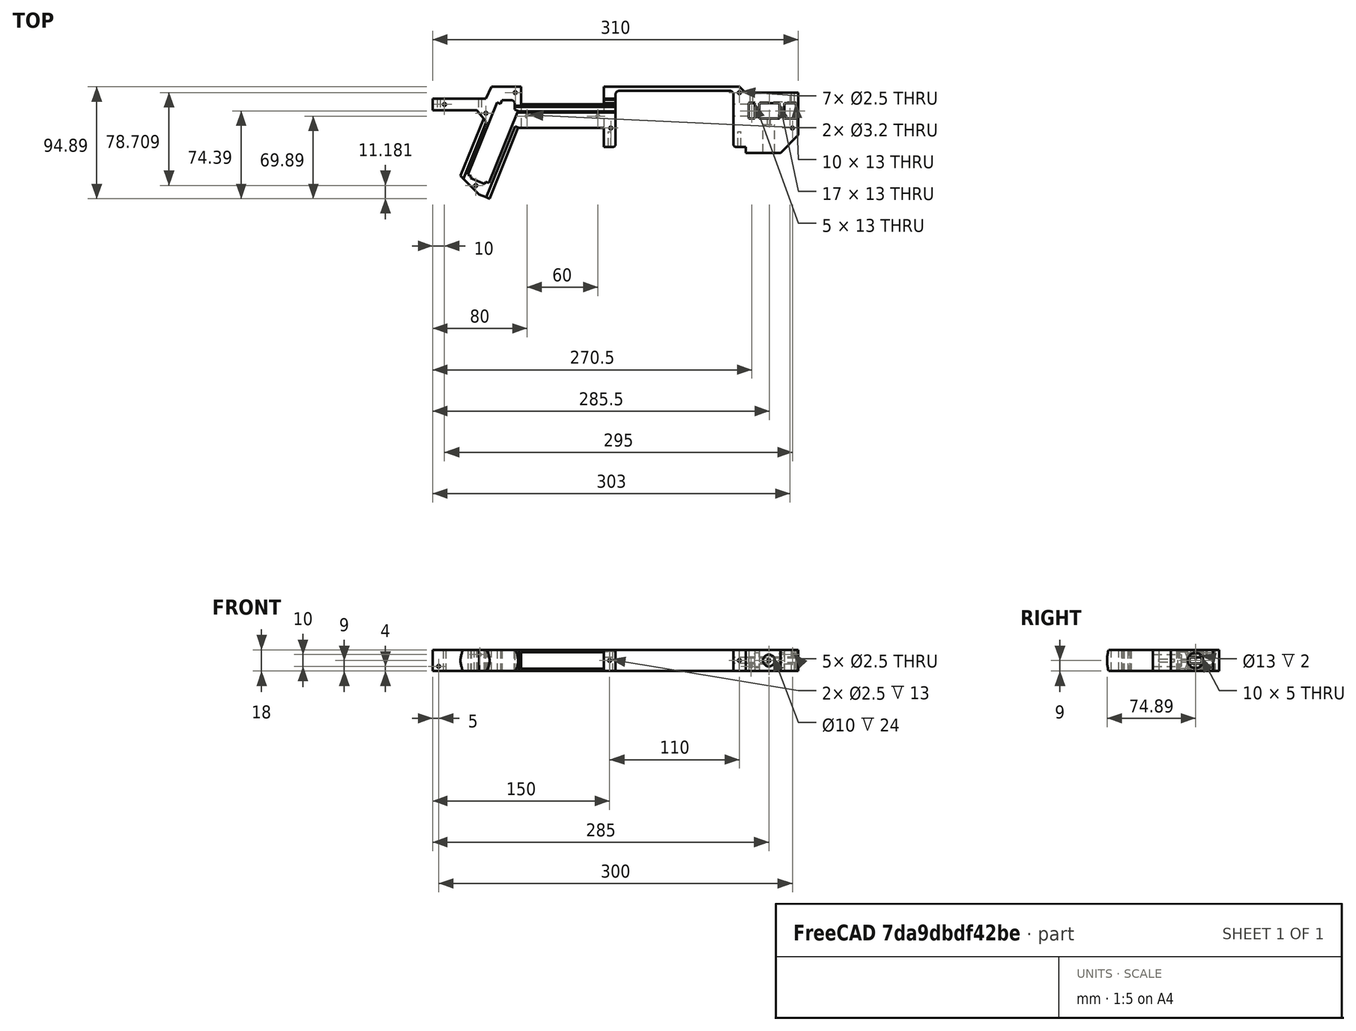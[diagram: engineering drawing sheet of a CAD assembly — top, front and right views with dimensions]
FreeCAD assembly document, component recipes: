
FREECAD ASSEMBLY — COMPONENT RECIPES ("FrameUpper.stl")

This assembly document has 2 components, labeled P0..P1 below (a component is one placed body or linked part). 1 of them carries a construction recipe — the FreeCAD feature program that regenerates the part from scratch, quoted from this document or its linked companion documents; the rest are supplied as boundary geometry only. No exploded tour is included for this assembly.
COMPONENT P0 — recipe-attached ("SizeRequirements", modeled in this document).
Construction recipe (the document's own serialized feature program — sketch geometry with constraints, then the solid features built on it; lengths are millimeters unless a unit is written):

FEATURE [Sketcher::SketchObject] Sketch
  ArcFitTolerance = 1e-06
  AttachmentSupport = -> [XY_Plane001]
  FullyConstrained = true
  MakeInternals = false
  MapMode = 5
  sketch-geometry (17):
    g0: LineSegment StartX=10 StartY=30 StartZ=0 EndX=10 EndY=15 EndZ=0
    g1: LineSegment StartX=10 StartY=15 StartZ=0 EndX=-60 EndY=15 EndZ=0
    g2: LineSegment StartX=-60 StartY=15 StartZ=0 EndX=-60 EndY=30 EndZ=0
    g3: LineSegment StartX=-60 StartY=30 StartZ=0 EndX=-85 EndY=30 EndZ=0
    g4: LineSegment StartX=-85 StartY=30 StartZ=0 EndX=-90 EndY=20 EndZ=0
    g5: LineSegment StartX=-90 StartY=20 StartZ=0 EndX=-135 EndY=20 EndZ=0
    g6: LineSegment StartX=-135 StartY=20 StartZ=0 EndX=-135 EndY=10 EndZ=0
    g7: LineSegment StartX=-135 StartY=10 StartZ=0 EndX=-60 EndY=10 EndZ=0
    g8: LineSegment StartX=-60 StartY=-5 StartZ=0 EndX=10 EndY=-5 EndZ=0
    g9: LineSegment StartX=125 StartY=30 StartZ=0 EndX=10 EndY=30 EndZ=0
    g10: LineSegment StartX=175 StartY=25 StartZ=0 EndX=130 EndY=25 EndZ=0
    g11: LineSegment StartX=130 StartY=25 StartZ=0 EndX=125 EndY=30 EndZ=0
    g12: LineSegment StartX=160 StartY=-26 StartZ=0 EndX=10 EndY=-26 EndZ=0
    g13: LineSegment StartX=10 StartY=-5 StartZ=0 EndX=10 EndY=-26 EndZ=0
    g14: LineSegment StartX=-60 StartY=-5 StartZ=0 EndX=-60 EndY=10 EndZ=0
    g15: LineSegment StartX=160 StartY=-26 StartZ=0 EndX=175 EndY=-11 EndZ=0
    g16: LineSegment StartX=175 StartY=-11 StartZ=0 EndX=175 EndY=25 EndZ=0
  constraints (51):
    c: Coincident(g0,g1)
    c: Horizontal(g1)
    c: Coincident(g1,g2)
    c: Coincident(g2,g3)
    c: Horizontal(g3)
    c: Coincident(g3,g4)
    c: Coincident(g4,g5)
    c: Horizontal(g5)
    c: Coincident(g5,g6)
    c: Coincident(g6,g7)
    c: Coincident(g9,g0)
    c: Horizontal(g9)
    c: Horizontal(g2,g0)
    c: DistanceX(g4,g3) = 5
    c: DistanceX(g3,g3) = 25
    c: DistanceY(g-1,g1) = 15
    c: DistanceY(g-1,g3) = 30
    c: Coincident(g10,g11)
    c: Coincident(g11,g9)
    c: DistanceY(g11,g11) = 5
    c: DistanceX(g11,g11) = 5
    c: DistanceX(g10,g10) = 45
    c: Horizontal(g10)
    c: DistanceX(g5,g5) = 45
    c: Vertical(g6)
    c: DistanceX(g-1,g10) = 175
    c: Horizontal(g7)
    c: Horizontal(g8)
    c: DistanceY(g8,g-1) = 5
    c: Horizontal(g12)
    c: DistanceY(g12,g-1) = 26
    c: Coincident(g13,g8)
    c: Coincident(g13,g12)
    c: Vertical(g2)
    c: Coincident(g14,g8)
    c: Vertical(g14)
    c: Coincident(g14,g7)
    c: DistanceY(g-1,g6) = 10
    c: DistanceY(g4,g4) = 10
    c: DistanceX(g1,g8) = 70
    c: DistanceX(g1,g-1) = 60
    c: DistanceX(g8,g1) = 0
    c: DistanceX(g1,g1) = 70
    c: Vertical(g0)
    c: Vertical(g13)
    c: Coincident(g15,g12)
    c: Coincident(g16,g15)
    c: Coincident(g16,g10)
    c: Vertical(g16)
    c: Angle(g15,g16) = 0.785398
    c: DistanceX(g12,g15) = 15
FEATURE [PartDesign::Pad] Pad
  Direction = (0,0,1)
  Length = 18
  Length2 = 10
  Midplane = true
  Profile = -> Sketch
  ReferenceAxis = -> Sketch [N_Axis]
  Refine = true
  Suppressed = false
  Type = 0
FEATURE [PartDesign::Plane] DatumPlane  label="HandgripRefBase"
  AttachmentOffset = pos=(0,97,50) rot=(-1,0,0;0.383972rad)
  AttachmentSupport = -> [Z_Axis001]
  Length = 75.4155
  MapMode = 2
  Placement = pos=(-97,-50,0) rot=(0.488067,-0.723589,0.488067;1.88883rad)
  ResizeMode = 0
  Width = 348.389
FEATURE [Sketcher::SketchObject] Sketch001
  ArcFitTolerance = 1e-06
  AttachmentSupport = -> [DatumPlane]
  FullyConstrained = true
  MakeInternals = false
  MapMode = 5
  Placement = pos=(-97,-50,0) rot=(0.488067,-0.723589,0.488067;1.88883rad)
  sketch-geometry (7):
    g0: LineSegment StartX=-9 StartY=12 StartZ=0 EndX=-9 EndY=-12 EndZ=0
    g1: LineSegment StartX=9 StartY=12 StartZ=0 EndX=9 EndY=-12 EndZ=0
    g2: ArcOfCircle CenterX=0 CenterY=4e-16 CenterZ=0 NormalX=0 NormalY=0 NormalZ=1 AngleXU=0 Radius=15 StartAngle=0.927295 EndAngle=2.2143
    g3: ArcOfCircle CenterX=0 CenterY=0 CenterZ=0 NormalX=0 NormalY=0 NormalZ=1 AngleXU=0 Radius=15 StartAngle=4.06889 EndAngle=5.35589
    g4: GeomPoint X=0 Y=15 Z=0
    g5: GeomPoint X=0 Y=-15 Z=0
    g6: Circle [constr] CenterX=0 CenterY=4e-16 CenterZ=0 NormalX=0 NormalY=0 NormalZ=1 AngleXU=0 Radius=15
  constraints (20):
    c: Vertical(g0)
    c: Vertical(g1)
    c: PointOnObject(g2,g-2)
    c: Coincident(g2,g0)
    c: Coincident(g2,g1)
    c: Coincident(g3,g1)
    c: Coincident(g3,g0)
    c: Equal(g3,g2)
    c: Distance(g0,g1) = 18
    c: Horizontal(g0,g1)
    c: PointOnObject(g4,g2)
    c: PointOnObject(g5,g3)
    c: Vertical(g5,g-1)
    c: Vertical(g-1,g4)
    c: DistanceY(g5,g4) = 30
    c: DistanceY(g1,g1) = 24
    c: Coincident(g6,g2)
    c: PointOnObject(g1,g6)
    c: PointOnObject(g0,g6)
    c: Coincident(g3,g-1)
FEATURE [PartDesign::Pad] Pad001  label="HadngripTube"
  BaseFeature = -> Pad
  Direction = (-0.374607,-0.927184,0)
  Length = 70
  Length2 = 10
  Profile = -> Sketch001
  ReferenceAxis = -> Sketch001 [N_Axis]
  Refine = true
  Reversed = true
  Suppressed = false
  Type = 4
FEATURE [PartDesign::Plane] DatumPlane001  label="HandgripRefFlat"
  AttachmentOffset = pos=(0,0,0) rot=(0,1,0;1.5708rad)
  AttachmentSupport = -> [DatumPlane]
  Length = 255.46
  MapMode = 5
  Placement = pos=(-97,-50,0) rot=(0,0,1;1.18682rad)
  ResizeMode = 0
  Width = 374.324
FEATURE [Sketcher::SketchObject] Sketch002
  ArcFitTolerance = 1e-06
  AttachmentSupport = -> [DatumPlane001]
  FullyConstrained = true
  MakeInternals = false
  MapMode = 5
  Placement = pos=(-97,-50,0) rot=(0,0,1;1.18682rad)
  sketch-geometry (14):
    g0: LineSegment StartX=2 StartY=-9.5 StartZ=0 EndX=68 EndY=-9.5 EndZ=0
    g1: LineSegment StartX=68 StartY=9.5 StartZ=0 EndX=2 EndY=9.5 EndZ=0
    g2: LineSegment StartX=2 StartY=9.5 StartZ=0 EndX=2 EndY=6.5 EndZ=0
    g3: LineSegment StartX=2 StartY=6.5 StartZ=0 EndX=0 EndY=6.5 EndZ=0
    g4: LineSegment StartX=0 StartY=6.5 StartZ=0 EndX=0 EndY=-6.5 EndZ=0
    g5: LineSegment StartX=0 StartY=-6.5 StartZ=0 EndX=2 EndY=-6.5 EndZ=0
    g6: LineSegment StartX=2 StartY=-6.5 StartZ=0 EndX=2 EndY=-9.5 EndZ=0
    g7: LineSegment StartX=68 StartY=-9.5 StartZ=0 EndX=68 EndY=-6.5 EndZ=0
    g8: LineSegment StartX=68 StartY=9.5 StartZ=0 EndX=68 EndY=6.5 EndZ=0
    g9: LineSegment StartX=68 StartY=6.5 StartZ=0 EndX=71.3759 EndY=6.5 EndZ=0
    g10: LineSegment StartX=71.3759 StartY=6.5 StartZ=0 EndX=74.2937 EndY=-0.721596 EndZ=0
    g11: LineSegment StartX=72.6359 StartY=-4.62697 StartZ=0 EndX=68 EndY=-6.5 EndZ=0
    g12: ArcOfCircle CenterX=71.5121 CenterY=-1.84542 CenterZ=0 NormalX=0 NormalY=0 NormalZ=1 AngleXU=0 Radius=3 StartAngle=5.09636 EndAngle=6.66716
    g13: GeomPoint [constr] X=75.4175 Y=-3.50315 Z=0
  constraints (39):
    c: Horizontal(g0)
    c: Horizontal(g1)
    c: Distance(g1,g0) = 19
    c: Symmetric(g0,g1,g-1)
    c: DistanceX(g0,g0) = 66
    c: Coincident(g2,g1)
    c: Vertical(g2)
    c: Coincident(g3,g2)
    c: PointOnObject(g3,g-2)
    c: Horizontal(g3)
    c: Coincident(g4,g3)
    c: PointOnObject(g4,g-2)
    c: Coincident(g5,g4)
    c: Coincident(g6,g5)
    c: Coincident(g6,g0)
    c: Horizontal(g5)
    c: Vertical(g6)
    c: Equal(g6,g2)
    c: DistanceY(g2,g2) = 3
    c: DistanceX(g5,g5) = 2
    c: Vertical(g1,g0)
    c: Coincident(g7,g0)
    c: Coincident(g8,g1)
    c: Equal(g2,g8)
    c: Equal(g8,g7)
    c: Vertical(g7)
    c: Vertical(g8)
    c: Coincident(g9,g8)
    c: Horizontal(g9)
    c: Coincident(g10,g9)
    c: Coincident(g11,g7)
    c: Perpendicular(g11,g10)
    c: Distance(g13,g11) = 8
    c: PointOnObject(g13,g10)
    c: PointOnObject(g13,g11)
    c: Tangent(g10,g12) = 1.5708
    c: Tangent(g11,g12) = 1.5708
    c: Radius(g12) = 3
    c: Angle(g-1,g11) = 0.383972
FEATURE [Sketcher::SketchObject] Sketch003
  ArcFitTolerance = 1e-06
  AttachmentSupport = -> [DatumPlane001]
  FullyConstrained = true
  MakeInternals = false
  MapMode = 5
  Placement = pos=(-97,-50,0) rot=(0,0,1;1.18682rad)
  sketch-geometry (6):
    g0: LineSegment StartX=55.4549 StartY=22.9123 StartZ=0 EndX=69.4915 EndY=-11.8294 EndZ=0
    g1: LineSegment StartX=55.5837 StartY=-17.4485 StartZ=0 EndX=55 EndY=-16.0038 EndZ=0
    g2: LineSegment StartX=69.4915 StartY=-11.8294 StartZ=0 EndX=55.5837 EndY=-17.4485 EndZ=0
    g3: LineSegment StartX=55 StartY=-16.0038 StartZ=0 EndX=55 EndY=0 EndZ=0
    g4: LineSegment StartX=55 StartY=0 StartZ=0 EndX=48 EndY=10 EndZ=0
    g5: LineSegment StartX=48 StartY=10 StartZ=0 EndX=55.4549 EndY=22.9123 EndZ=0
  constraints (19):
    c: PointOnObject(g0,g-4)
    c: DistanceX(g-1,g1) = 55
    c: Coincident(g1,g-3)
    c: Coincident(g2,g0)
    c: Coincident(g2,g1)
    c: Perpendicular(g2,g0)
    c: Parallel(g0,g-4)
    c: Parallel(g-3,g1)
    c: DistanceY(g1,g-1) = 16.0038
    c: DistanceY(g-1,g0) = 22.9123
    c: Coincident(g4,g3)
    c: Coincident(g5,g4)
    c: DistanceY(g-1,g4) = 10
    c: PointOnObject(g3,g-1)
    c: Angle(g5,g-1) = 2.0944
    c: DistanceX(g-1,g4) = 48
    c: Coincident(g0,g5)
    c: Coincident(g3,g1)
    c: Vertical(g3)
FEATURE [PartDesign::Pad] Pad002  label="HandgripEndstop"
  BaseFeature = -> Pad001
  Direction = (0,0,1)
  Length = 18
  Length2 = 10
  Midplane = true
  Profile = -> Sketch003
  ReferenceAxis = -> Sketch003 [N_Axis]
  Refine = true
  Suppressed = false
  Type = 0
FEATURE [PartDesign::Pocket] Pocket  label="18650Cutout"
  BaseFeature = -> Pad002
  Direction = (0,0,-1)
  Length = 9
  Length2 = 100
  Midplane = true
  Profile = -> Sketch002
  ReferenceAxis = -> Sketch002 [N_Axis]
  Refine = true
  Suppressed = false
  Type = 1
FEATURE [Sketcher::SketchObject] Sketch004
  ArcFitTolerance = 1e-06
  AttachmentSupport = -> [DatumPlane001]
  FullyConstrained = true
  MakeInternals = false
  MapMode = 5
  Placement = pos=(-97,-50,0) rot=(0,0,1;1.18682rad)
  sketch-geometry (2):
    g0: Circle CenterX=-4 CenterY=0 CenterZ=0 NormalX=0 NormalY=0 NormalZ=1 AngleXU=0 Radius=1.25
    g1: Circle CenterX=56 CenterY=15 CenterZ=0 NormalX=0 NormalY=0 NormalZ=1 AngleXU=0 Radius=1.25
  constraints (6):
    c: PointOnObject(g0,g-1)
    c: Diameter(g0) = 2.5
    c: DistanceX(g0,g-1) = 4
    c: Equal(g1,g0)
    c: DistanceY(g-1,g1) = 15
    c: DistanceX(g0,g1) = 60
FEATURE [Sketcher::SketchObject] Sketch005
  ArcFitTolerance = 1e-06
  AttachmentSupport = -> [XY_Plane001]
  FullyConstrained = true
  MakeInternals = false
  MapMode = 5
  sketch-geometry (3):
    g0: LineSegment StartX=-122 StartY=-35 StartZ=0 EndX=-82 EndY=-75 EndZ=0
    g1: LineSegment StartX=-82 StartY=-75 StartZ=0 EndX=-122 EndY=-75 EndZ=0
    g2: LineSegment StartX=-122 StartY=-75 StartZ=0 EndX=-122 EndY=-35 EndZ=0
  constraints (9):
    c: Coincident(g1,g0)
    c: Horizontal(g1)
    c: Coincident(g2,g1)
    c: Coincident(g2,g0)
    c: Vertical(g2)
    c: Angle(g2,g0) = 0.785398
    c: DistanceX(g0,g-1) = 122
    c: DistanceY(g0,g-1) = 35
    c: DistanceX(g1,g1) = 40
FEATURE [PartDesign::Pocket] Pocket002  label="HandgripPrintbedAdjust"
  BaseFeature = -> Pocket
  Direction = (0,0,-1)
  Length = 5
  Length2 = 5
  Midplane = true
  Profile = -> Sketch005
  ReferenceAxis = -> Sketch005 [N_Axis]
  Refine = true
  Suppressed = false
  Type = 1
FEATURE [PartDesign::Pocket] Pocket003  label="HandgripRetainingScrews"
  BaseFeature = -> Pocket002
  Direction = (0,0,-1)
  Length = 5
  Length2 = 5
  Midplane = true
  Profile = -> Sketch004
  ReferenceAxis = -> Sketch004 [N_Axis]
  Refine = true
  Suppressed = false
  Type = 1
FEATURE [Sketcher::SketchObject] Sketch006
  ArcFitTolerance = 1e-06
  AttachmentOffset = pos=(0,0,-26) rot=(0,0,1;0rad)
  AttachmentSupport = -> [XZ_Plane001]
  FullyConstrained = true
  MakeInternals = false
  MapMode = 5
  Placement = pos=(0,26,-5.8e-15) rot=(1,0,0;1.5708rad)
  sketch-geometry (4):
    g0: LineSegment StartX=-60 StartY=7 StartZ=0 EndX=-60 EndY=-7 EndZ=0
    g1: LineSegment StartX=-60 StartY=-7 StartZ=0 EndX=10 EndY=-7 EndZ=0
    g2: LineSegment StartX=10 StartY=-7 StartZ=0 EndX=10 EndY=7 EndZ=0
    g3: LineSegment StartX=10 StartY=7 StartZ=0 EndX=-60 EndY=7 EndZ=0
  constraints (11):
    c: Coincident(g0,g1)
    c: Coincident(g1,g2)
    c: Coincident(g2,g3)
    c: Coincident(g3,g0)
    c: Vertical(g2)
    c: Horizontal(g1)
    c: Horizontal(g3)
    c: DistanceX(g0,g-1) = 60
    c: Distance(g0,g0) = 14
    c: Symmetric(g0,g0,g-1)
    c: DistanceX(g-1,g1) = 10
FEATURE [PartDesign::Pocket] Pocket004  label="TriggerSlot"
  BaseFeature = -> Pocket003
  Direction = (0,1,-2e-16)
  Length = 5
  Length2 = 5
  Profile = -> Sketch006
  ReferenceAxis = -> Sketch006 [N_Axis]
  Refine = true
  Reversed = true
  Suppressed = false
  Type = 1
FEATURE [Sketcher::SketchObject] Sketch007
  ArcFitTolerance = 1e-06
  AttachmentSupport = -> [XY_Plane001]
  FullyConstrained = true
  MakeInternals = false
  MapMode = 5
  sketch-geometry (2):
    g0: Circle CenterX=-55 CenterY=5 CenterZ=0 NormalX=0 NormalY=0 NormalZ=1 AngleXU=0 Radius=1.6
    g1: Circle CenterX=5 CenterY=5 CenterZ=0 NormalX=0 NormalY=0 NormalZ=1 AngleXU=0 Radius=1.6
  constraints (6):
    c: Equal(g0,g1)
    c: Diameter(g1) = 3.2
    c: DistanceX(g0,g1) = 60
    c: DistanceX(g-1,g1) = 5
    c: DistanceY(g-1,g1) = 5
    c: Horizontal(g1,g0)
FEATURE [PartDesign::Pocket] Pocket005  label="TriggerRetainingScrews"
  BaseFeature = -> Pocket004
  Direction = (0,0,-1)
  Length = 5
  Length2 = 5
  Profile = -> Sketch007
  ReferenceAxis = -> Sketch007 [N_Axis]
  Refine = true
  Suppressed = false
  Type = 1
FEATURE [Sketcher::SketchObject] Sketch008
  ArcFitTolerance = 1e-06
  AttachmentOffset = pos=(0,0,173) rot=(0,0,1;0rad)
  AttachmentSupport = -> [YZ_Plane001]
  FullyConstrained = true
  MakeInternals = false
  MapMode = 5
  Placement = pos=(173,0,0) rot=(0.57735,0.57735,0.57735;2.0944rad)
  sketch-geometry (7):
    g0: Circle [constr] CenterX=10 CenterY=0 CenterZ=0 NormalX=0 NormalY=0 NormalZ=1 AngleXU=0 Radius=6.25
    g1: LineSegment StartX=12.5888 StartY=-6.25 StartZ=0 EndX=17 EndY=-1.83883 EndZ=0
    g2: LineSegment StartX=17 StartY=-1.83883 StartZ=0 EndX=17 EndY=1.83883 EndZ=0
    g3: LineSegment StartX=17 StartY=1.83883 StartZ=0 EndX=12.5888 EndY=6.25 EndZ=0
    g4: LineSegment StartX=12.5888 StartY=-6.25 StartZ=0 EndX=3.75 EndY=-6.25 EndZ=0
    g5: LineSegment StartX=12.5888 StartY=6.25 StartZ=0 EndX=3.75 EndY=6.25 EndZ=0
    g6: LineSegment StartX=3.75 StartY=6.25 StartZ=0 EndX=3.75 EndY=-6.25 EndZ=0
  constraints (19):
    c: Diameter(g0) = 12.5
    c: PointOnObject(g0,g-1)
    c: DistanceX(g-1,g0) = 10
    c: Coincident(g1,g2)
    c: Coincident(g2,g3)
    c: Angle(g2,g3) = 0.785398
    c: Symmetric(g1,g2,g-1)
    c: Symmetric(g1,g3,g-1)
    c: Tangent(g3,g0)
    c: DistanceX(g0,g1) = 7
    c: Coincident(g4,g1)
    c: Coincident(g5,g3)
    c: Horizontal(g5)
    c: Coincident(g6,g5)
    c: Coincident(g6,g4)
    c: Vertical(g6)
    c: Horizontal(g4)
    c: Tangent(g5,g0)
    c: Tangent(g6,g0)
FEATURE [PartDesign::Pocket] Pocket006  label="LaserCutout"
  BaseFeature = -> Pocket005
  Direction = (-1,0,0)
  Length = 40
  Length2 = 5
  Profile = -> Sketch008
  ReferenceAxis = -> Sketch008 [N_Axis]
  Refine = true
  Suppressed = false
  Type = 0
FEATURE [Sketcher::SketchObject] Sketch009
  ArcFitTolerance = 1e-06
  AttachmentSupport = -> [XY_Plane001]
  FullyConstrained = true
  MakeInternals = false
  MapMode = 5
  sketch-geometry (14):
    g0: LineSegment StartX=133 StartY=16 StartZ=0 EndX=133 EndY=3 EndZ=0
    g1: LineSegment StartX=173 StartY=3 StartZ=0 EndX=173 EndY=16 EndZ=0
    g2: LineSegment StartX=173 StartY=16 StartZ=0 EndX=163 EndY=16 EndZ=0
    g3: LineSegment StartX=163 StartY=16 StartZ=0 EndX=163 EndY=3 EndZ=0
    g4: LineSegment [constr] StartX=163 StartY=3 StartZ=0 EndX=159 EndY=3 EndZ=0
    g5: LineSegment StartX=159 StartY=3 StartZ=0 EndX=159 EndY=16 EndZ=0
    g6: LineSegment StartX=159 StartY=16 StartZ=0 EndX=142 EndY=16 EndZ=0
    g7: LineSegment StartX=142 StartY=16 StartZ=0 EndX=142 EndY=3 EndZ=0
    g8: LineSegment [constr] StartX=142 StartY=3 StartZ=0 EndX=138 EndY=3 EndZ=0
    g9: LineSegment StartX=138 StartY=3 StartZ=0 EndX=138 EndY=16 EndZ=0
    g10: LineSegment StartX=138 StartY=16 StartZ=0 EndX=133 EndY=16 EndZ=0
    g11: LineSegment StartX=133 StartY=3 StartZ=0 EndX=138 EndY=3 EndZ=0
    g12: LineSegment StartX=159 StartY=3 StartZ=0 EndX=142 EndY=3 EndZ=0
    g13: LineSegment StartX=163 StartY=3 StartZ=0 EndX=173 EndY=3 EndZ=0
  constraints (40):
    c: Vertical(g0)
    c: Coincident(g1,g2)
    c: Horizontal(g2)
    c: Coincident(g2,g3)
    c: Vertical(g3)
    c: Coincident(g3,g4)
    c: Coincident(g4,g5)
    c: Vertical(g5)
    c: Coincident(g5,g6)
    c: Horizontal(g6)
    c: Coincident(g6,g7)
    c: Coincident(g7,g8)
    c: Horizontal(g8)
    c: Coincident(g8,g9)
    c: Vertical(g9)
    c: Coincident(g9,g10)
    c: Coincident(g10,g0)
    c: Horizontal(g10)
    c: Horizontal(g5,g2)
    c: Horizontal(g6,g9)
    c: DistanceY(g-1,g1) = 16
    c: Vertical(g1)
    c: DistanceX(g-1,g1) = 173
    c: DistanceY(g-1,g1) = 3
    c: Horizontal(g4)
    c: Equal(g4,g8)
    c: DistanceX(g8,g8) = 4
    c: Horizontal(g7,g4)
    c: DistanceX(g2,g2) = 10
    c: DistanceX(g10,g10) = 5
    c: DistanceX(g0,g1) = 40
    c: Vertical(g7)
    c: Coincident(g11,g0)
    c: Coincident(g11,g8)
    c: Coincident(g12,g4)
    c: Coincident(g12,g7)
    c: Coincident(g13,g3)
    c: Coincident(g13,g1)
    c: Horizontal(g13)
    c: Horizontal(g11)
FEATURE [PartDesign::Pocket] Pocket007  label="LaserCutout2"
  BaseFeature = -> Pocket006
  Direction = (0,0,-1)
  Length = 5
  Length2 = 5
  Midplane = true
  Profile = -> Sketch009
  ReferenceAxis = -> Sketch009 [N_Axis]
  Refine = true
  Suppressed = false
  Type = 1
FEATURE [Sketcher::SketchObject] Sketch010
  ArcFitTolerance = 1e-06
  AttachmentOffset = pos=(0,0,165) rot=(0,0,1;0rad)
  AttachmentSupport = -> [YZ_Plane001]
  FullyConstrained = true
  MakeInternals = false
  MapMode = 5
  Placement = pos=(165,0,0) rot=(0.57735,0.57735,0.57735;2.0944rad)
  sketch-geometry (1):
    g0: Circle CenterX=10 CenterY=0 CenterZ=0 NormalX=0 NormalY=0 NormalZ=1 AngleXU=0 Radius=6.5
  constraints (3):
    c: PointOnObject(g0,g-1)
    c: Diameter(g0) = 13
    c: DistanceX(g-1,g0) = 10
FEATURE [PartDesign::Pocket] Pocket008  label="LaserEmitterHole"
  BaseFeature = -> Pocket007
  Direction = (-1,0,0)
  Length = 5
  Length2 = 5
  Profile = -> Sketch010
  ReferenceAxis = -> Sketch010 [N_Axis]
  Refine = true
  Reversed = true
  Suppressed = false
  Type = 1
FEATURE [Sketcher::SketchObject] Sketch011
  ArcFitTolerance = 1e-06
  AttachmentOffset = pos=(0,0,45) rot=(0,0,1;0rad)
  AttachmentSupport = -> [XZ_Plane001]
  FullyConstrained = true
  MakeInternals = false
  MapMode = 5
  Placement = pos=(0,-45,1e-14) rot=(1,0,0;1.5708rad)
  sketch-geometry (1):
    g0: Circle CenterX=150 CenterY=0 CenterZ=0 NormalX=0 NormalY=0 NormalZ=1 AngleXU=0 Radius=1.5
  constraints (3):
    c: PointOnObject(g0,g-1)
    c: Diameter(g0) = 3
    c: DistanceX(g-1,g0) = 150
FEATURE [PartDesign::Hole] Hole  label="LaserRetainingScrew"
  BaseFeature = -> Pocket008
  CustomThreadClearance = 0
  Depth = 55
  DepthType = 0
  Diameter = 2.5
  DrillForDepth = false
  DrillPoint = 1
  DrillPointAngle = 118
  HoleCutCountersinkAngle = 90
  HoleCutCustomValues = false
  HoleCutDepth = 43
  HoleCutDiameter = 10
  HoleCutType = 1
  ModelThread = false
  Profile = -> Sketch011
  Refine = true
  Suppressed = false
  Tapered = false
  TaperedAngle = 90
  ThreadClass = 0
  ThreadDepth = 55
  ThreadDepthType = 0
  ThreadDirection = 0
  ThreadFit = 0
  ThreadSize = 0
  ThreadType = 0
  Threaded = false
  UseCustomThreadClearance = false
FEATURE [Sketcher::SketchObject] Sketch012
  ArcFitTolerance = 1e-06
  AttachmentOffset = pos=(0,0,135) rot=(0,0,1;0rad)
  AttachmentSupport = -> [YZ_Plane001]
  FullyConstrained = true
  MakeInternals = false
  MapMode = 5
  Placement = pos=(135,0,0) rot=(0.57735,0.57735,0.57735;2.0944rad)
  sketch-geometry (6):
    g0: LineSegment StartX=5 StartY=2.5 StartZ=0 EndX=5 EndY=-2.5 EndZ=0
    g1: LineSegment StartX=5 StartY=-2.5 StartZ=0 EndX=15 EndY=-2.5 EndZ=0
    g2: LineSegment StartX=15 StartY=-2.5 StartZ=0 EndX=15 EndY=2.5 EndZ=0
    g3: LineSegment StartX=15 StartY=2.5 StartZ=0 EndX=5 EndY=2.5 EndZ=0
    g4: GeomPoint X=10 Y=2.5 Z=0
    g5: GeomPoint X=15 Y=0 Z=0
  constraints (14):
    c: Coincident(g0,g1)
    c: Coincident(g1,g2)
    c: Coincident(g2,g3)
    c: Coincident(g3,g0)
    c: Vertical(g0)
    c: Vertical(g2)
    c: Horizontal(g1)
    c: Horizontal(g3)
    c: DistanceX(g3,g3) = 10
    c: Distance(g0,g0) = 5
    c: Symmetric(g3,g3,g4)
    c: DistanceX(g-1,g4) = 10
    c: Symmetric(g2,g2,g5)
    c: PointOnObject(g5,g-1)
FEATURE [PartDesign::Pocket] Pocket009  label="LaserWireRoute"
  BaseFeature = -> Hole
  Direction = (-1,0,0)
  Length = 30
  Length2 = 5
  Profile = -> Sketch012
  ReferenceAxis = -> Sketch012 [N_Axis]
  Refine = true
  Suppressed = false
  Type = 0
FEATURE [Sketcher::SketchObject] Sketch013
  ArcFitTolerance = 1e-06
  AttachmentSupport = -> [XY_Plane001]
  FullyConstrained = true
  MakeInternals = false
  MapMode = 5
  sketch-geometry (16):
    g0: LineSegment StartX=20 StartY=23.5 StartZ=0 EndX=20 EndY=-19 EndZ=0
    g1: LineSegment StartX=120 StartY=-19 StartZ=0 EndX=120 EndY=23.5 EndZ=0
    g2: LineSegment StartX=117 StartY=26.5 StartZ=0 EndX=23 EndY=26.5 EndZ=0
    g3: ArcOfCircle CenterX=23 CenterY=23.5 CenterZ=0 NormalX=0 NormalY=0 NormalZ=1 AngleXU=0 Radius=3 StartAngle=1.5708 EndAngle=3.14159
    g4: GeomPoint [constr] X=20 Y=26.5 Z=0
    g5: ArcOfCircle CenterX=117 CenterY=23.5 CenterZ=0 NormalX=0 NormalY=0 NormalZ=1 AngleXU=0 Radius=3 StartAngle=0 EndAngle=1.5708
    g6: GeomPoint [constr] X=120 Y=26.5 Z=0
    g7: LineSegment StartX=18 StartY=-21 StartZ=0 EndX=10 EndY=-21 EndZ=0
    g8: LineSegment StartX=10 StartY=-21 StartZ=0 EndX=10 EndY=-26 EndZ=0
    g9: LineSegment StartX=10 StartY=-26 StartZ=0 EndX=130.5 EndY=-26 EndZ=0
    g10: LineSegment StartX=130.5 StartY=-26 StartZ=0 EndX=130.5 EndY=-21 EndZ=0
    g11: LineSegment StartX=130.5 StartY=-21 StartZ=0 EndX=122 EndY=-21 EndZ=0
    g12: ArcOfCircle CenterX=18 CenterY=-19 CenterZ=0 NormalX=0 NormalY=0 NormalZ=1 AngleXU=0 Radius=2 StartAngle=4.71239 EndAngle=6.28319
    g13: GeomPoint [constr] X=20 Y=-21 Z=0
    g14: ArcOfCircle CenterX=122 CenterY=-19 CenterZ=0 NormalX=0 NormalY=0 NormalZ=1 AngleXU=0 Radius=2 StartAngle=3.14159 EndAngle=4.71239
    g15: GeomPoint [constr] X=120 Y=-21 Z=0
  constraints (42):
    c: Vertical(g0)
    c: Vertical(g1)
    c: Horizontal(g2)
    c: PointOnObject(g4,g0)
    c: PointOnObject(g4,g2)
    c: Tangent(g0,g3) = -1.5708
    c: Tangent(g2,g3) = -1.5708
    c: PointOnObject(g6,g1)
    c: PointOnObject(g6,g2)
    c: Tangent(g1,g5) = -1.5708
    c: Tangent(g2,g5) = -1.5708
    c: Equal(g3,g5)
    c: Radius(g5) = 3
    c: DistanceY(g-1,g2) = 26.5
    c: DistanceX(g-1,g13) = 20
    c: DistanceX(g0,g1) = 100
    c: Horizontal(g7)
    c: Coincident(g8,g7)
    c: Coincident(g9,g8)
    c: Horizontal(g9)
    c: Coincident(g10,g9)
    c: Vertical(g10)
    c: Coincident(g11,g10)
    c: Horizontal(g11)
    c: Vertical(g8)
    c: Horizontal(g13,g15)
    c: DistanceX(g7,g13) = 10
    c: DistanceY(g8,g-1) = 26
    c: PointOnObject(g13,g0)
    c: PointOnObject(g13,g7)
    c: Tangent(g0,g12) = 1.5708
    c: Tangent(g7,g12) = 1.5708
    c: PointOnObject(g15,g1)
    c: PointOnObject(g15,g11)
    c: Tangent(g1,g14) = 1.5708
    c: Tangent(g11,g14) = 1.5708
    c: Equal(g14,g12)
    c: Radius(g12) = 2
    c: DistanceX(g15,g10) = 10.5
    c: DistanceY(g9,g2) = 52.5
    c: DistanceY(g10,g6) = 47.5
    c: DistanceY(g8,g7) = 5
FEATURE [PartDesign::Pocket] Pocket010  label="ElectronicsBayCutout"
  BaseFeature = -> Pocket009
  Direction = (0,0,-1)
  Length = 5
  Length2 = 5
  Midplane = true
  Profile = -> Sketch013
  ReferenceAxis = -> Sketch013 [N_Axis]
  Refine = true
  Suppressed = false
  Type = 1
FEATURE [Sketcher::SketchObject] Sketch014
  ArcFitTolerance = 1e-06
  AttachmentOffset = pos=(0,0,9) rot=(0,0,1;0rad)
  AttachmentSupport = -> [XY_Plane001]
  FullyConstrained = true
  MakeInternals = false
  MapMode = 5
  Placement = pos=(0,0,9) rot=(0,0,1;0rad)
  sketch-geometry (4):
    g0: LineSegment StartX=-70 StartY=14 StartZ=0 EndX=-70 EndY=8 EndZ=0
    g1: LineSegment StartX=-70 StartY=8 StartZ=0 EndX=30 EndY=8 EndZ=0
    g2: LineSegment StartX=30 StartY=8 StartZ=0 EndX=30 EndY=14 EndZ=0
    g3: LineSegment StartX=30 StartY=14 StartZ=0 EndX=-70 EndY=14 EndZ=0
  constraints (12):
    c: Coincident(g0,g1)
    c: Coincident(g1,g2)
    c: Coincident(g2,g3)
    c: Coincident(g3,g0)
    c: Vertical(g0)
    c: Vertical(g2)
    c: Horizontal(g1)
    c: Horizontal(g3)
    c: DistanceY(g2,g2) = 6
    c: DistanceX(g0,g-1) = 70
    c: DistanceY(g-1,g1) = 8
    c: DistanceX(g-1,g2) = 30
FEATURE [PartDesign::Pocket] Pocket011  label="BatteryWireCutout"
  BaseFeature = -> Pocket010
  Direction = (0,0,-1)
  Length = 1.2
  Length2 = 5
  Profile = -> Sketch014
  ReferenceAxis = -> Sketch014 [N_Axis]
  Refine = true
  Suppressed = false
  TaperAngle = -45
  Type = 0
FEATURE [Sketcher::SketchObject] Sketch015
  ArcFitTolerance = 1e-06
  AttachmentOffset = pos=(0,0,10) rot=(0,0,1;0rad)
  AttachmentSupport = -> [XY_Plane001]
  FullyConstrained = true
  MakeInternals = false
  MapMode = 5
  Placement = pos=(0,0,10) rot=(0,0,1;0rad)
  sketch-geometry (5):
    g0: Circle CenterX=170 CenterY=-5 CenterZ=0 NormalX=0 NormalY=0 NormalZ=1 AngleXU=0 Radius=1.25
    g1: Circle CenterX=16 CenterY=-5 CenterZ=0 NormalX=0 NormalY=0 NormalZ=1 AngleXU=0 Radius=1.25
    g2: Circle CenterX=-65 CenterY=25 CenterZ=0 NormalX=0 NormalY=0 NormalZ=1 AngleXU=0 Radius=1.25
    g3: Circle CenterX=-125 CenterY=15 CenterZ=0 NormalX=0 NormalY=0 NormalZ=1 AngleXU=0 Radius=1.25
    g4: Circle CenterX=125 CenterY=25 CenterZ=0 NormalX=0 NormalY=0 NormalZ=1 AngleXU=0 Radius=1.25
  constraints (15):
    c: Equal(g3,g2)
    c: Equal(g2,g1)
    c: Equal(g1,g0)
    c: Diameter(g3) = 2.5
    c: DistanceX(g3,g-1) = 125
    c: DistanceY(g-1,g3) = 15
    c: DistanceY(g-1,g2) = 25
    c: DistanceX(g2,g-1) = 65
    c: DistanceX(g-1,g1) = 16
    c: DistanceY(g1,g-1) = 5
    c: Horizontal(g1,g0)
    c: DistanceX(g-1,g0) = 170
    c: DistanceX(g-1,g4) = 125
    c: DistanceY(g-1,g4) = 25
    c: Equal(g4,g0)
FEATURE [Sketcher::SketchObject] Sketch016
  ArcFitTolerance = 1e-06
  AttachmentOffset = pos=(0,0,-25) rot=(0,0,1;0rad)
  AttachmentSupport = -> [XZ_Plane001]
  FullyConstrained = true
  MakeInternals = false
  MapMode = 5
  Placement = pos=(0,25,-5.6e-15) rot=(1,0,0;1.5708rad)
  sketch-geometry (3):
    g0: Circle CenterX=135 CenterY=-5 CenterZ=0 NormalX=0 NormalY=0 NormalZ=1 AngleXU=0 Radius=1.25
    g1: Circle CenterX=170 CenterY=5 CenterZ=0 NormalX=0 NormalY=0 NormalZ=1 AngleXU=0 Radius=1.25
    g2: LineSegment [constr] StartX=175 StartY=-9 StartZ=0 EndX=175 EndY=9 EndZ=0
  constraints (10):
    c: DistanceY(g-1,g1) = 5
    c: DistanceY(g0,g-1) = 5
    c: Diameter(g0) = 2.5
    c: Symmetric(g2,g2,g-1)
    c: Distance(g2,g2) = 18
    c: DistanceX(g-1,g2) = 175
    c: DistanceX(g1,g2) = 5
    c: DistanceX(g0,g2) = 40
    c: DistanceY(g1,g2) = 4
    c: Equal(g1,g0)
FEATURE [Sketcher::SketchObject] Sketch018
  ArcFitTolerance = 1e-06
  AttachmentOffset = pos=(0,0,-20) rot=(0,0,1;0rad)
  AttachmentSupport = -> [XZ_Plane001]
  FullyConstrained = true
  MakeInternals = false
  MapMode = 5
  Placement = pos=(0,20,-4.4e-15) rot=(1,0,0;1.5708rad)
  sketch-geometry (3):
    g0: Circle CenterX=-130 CenterY=-5 CenterZ=0 NormalX=0 NormalY=0 NormalZ=1 AngleXU=0 Radius=1.25
    g1: Circle CenterX=-95 CenterY=5 CenterZ=0 NormalX=0 NormalY=0 NormalZ=1 AngleXU=0 Radius=1.25
    g2: LineSegment [constr] StartX=-135 StartY=9 StartZ=0 EndX=-135 EndY=-9 EndZ=0
  constraints (9):
    c: Equal(g0,g1)
    c: DistanceY(g2,g2) = 18
    c: Symmetric(g2,g2,g-1)
    c: DistanceX(g2,g-1) = 135
    c: DistanceX(g2,g0) = 5
    c: Distance(g0,g-1) = 5
    c: Distance(g1,g-1) = 5
    c: Diameter(g0) = 2.5
    c: DistanceX(g2,g1) = 40
FEATURE [Sketcher::SketchObject] Sketch020
  ArcFitTolerance = 1e-06
  AttachmentOffset = pos=(0,0,9) rot=(0,0,1;0rad)
  AttachmentSupport = -> [XY_Plane001]
  FullyConstrained = true
  MakeInternals = false
  MapMode = 5
  Placement = pos=(0,0,9) rot=(0,0,1;0rad)
  sketch-geometry (4):
    g0: LineSegment StartX=7 StartY=20 StartZ=0 EndX=7 EndY=15 EndZ=0
    g1: LineSegment StartX=7 StartY=15 StartZ=0 EndX=27 EndY=15 EndZ=0
    g2: LineSegment StartX=27 StartY=15 StartZ=0 EndX=27 EndY=20 EndZ=0
    g3: LineSegment StartX=27 StartY=20 StartZ=0 EndX=7 EndY=20 EndZ=0
  constraints (12):
    c: Coincident(g0,g1)
    c: Coincident(g1,g2)
    c: Coincident(g2,g3)
    c: Coincident(g3,g0)
    c: Vertical(g0)
    c: Vertical(g2)
    c: Horizontal(g1)
    c: Horizontal(g3)
    c: DistanceY(g0,g0) = 5
    c: DistanceY(g-1,g0) = 20
    c: DistanceX(g-1,g0) = 7
    c: DistanceX(g3,g3) = 20
FEATURE [PartDesign::Pocket] Pocket013  label="TriggerloadingWireCutout"
  BaseFeature = -> Pocket011
  Direction = (0,0,-1)
  Length = 6
  Length2 = 5
  Profile = -> Sketch020
  ReferenceAxis = -> Sketch020 [N_Axis]
  Refine = true
  Suppressed = false
  TaperAngle = -10
  Type = 0
FEATURE [PartDesign::Hole] Hole001  label="SidePlateRetainingScrews"
  BaseFeature = -> Pocket013
  CustomThreadClearance = 0
  Depth = 656.003
  DepthType = 1
  Diameter = 2.5
  DrillForDepth = false
  DrillPoint = 1
  DrillPointAngle = 118
  HoleCutCountersinkAngle = 90
  HoleCutCustomValues = false
  HoleCutDepth = 0
  HoleCutDiameter = 6.1
  HoleCutType = 0
  ModelThread = false
  Profile = -> Sketch015
  Refine = true
  Suppressed = false
  Tapered = false
  TaperedAngle = 90
  ThreadClass = 0
  ThreadDepth = 656.003
  ThreadDepthType = 0
  ThreadDirection = 0
  ThreadFit = 0
  ThreadSize = 0
  ThreadType = 0
  Threaded = false
  UseCustomThreadClearance = false
FEATURE [PartDesign::Hole] Hole002  label="FrontSightRetainingScrews"
  BaseFeature = -> Hole001
  CustomThreadClearance = 0
  Depth = 10
  DepthType = 0
  Diameter = 2.5
  DrillForDepth = false
  DrillPoint = 0
  DrillPointAngle = 118
  HoleCutCountersinkAngle = 90
  HoleCutCustomValues = false
  HoleCutDepth = 0
  HoleCutDiameter = 6.1
  HoleCutType = 0
  ModelThread = false
  Profile = -> Sketch016
  Refine = true
  Reversed = true
  Suppressed = false
  Tapered = false
  TaperedAngle = 90
  ThreadClass = 0
  ThreadDepth = 10
  ThreadDepthType = 0
  ThreadDirection = 0
  ThreadFit = 0
  ThreadSize = 0
  ThreadType = 0
  Threaded = false
  UseCustomThreadClearance = false
FEATURE [PartDesign::Hole] Hole003  label="RearSightRetainingScrews"
  BaseFeature = -> Hole002
  CustomThreadClearance = 0
  Depth = 20
  DepthType = 0
  Diameter = 2.5
  DrillForDepth = false
  DrillPoint = 0
  DrillPointAngle = 118
  HoleCutCountersinkAngle = 90
  HoleCutCustomValues = false
  HoleCutDepth = 0
  HoleCutDiameter = 6.1
  HoleCutType = 0
  ModelThread = false
  Profile = -> Sketch018
  Refine = true
  Reversed = true
  Suppressed = false
  Tapered = false
  TaperedAngle = 90
  ThreadClass = 0
  ThreadDepth = 20
  ThreadDepthType = 0
  ThreadDirection = 0
  ThreadFit = 0
  ThreadSize = 0
  ThreadType = 0
  Threaded = false
  UseCustomThreadClearance = false
FEATURE [Sketcher::SketchObject] Sketch021
  ArcFitTolerance = 1e-06
  AttachmentOffset = pos=(0,0,22) rot=(0,0,1;0rad)
  AttachmentSupport = -> [XZ_Plane001]
  FullyConstrained = true
  MakeInternals = false
  MapMode = 5
  Placement = pos=(0,-22,4.9e-15) rot=(1,0,0;1.5708rad)
  sketch-geometry (2):
    g0: Circle CenterX=15 CenterY=0 CenterZ=0 NormalX=0 NormalY=0 NormalZ=1 AngleXU=0 Radius=1.5
    g1: Circle CenterX=125 CenterY=0 CenterZ=0 NormalX=0 NormalY=0 NormalZ=1 AngleXU=0 Radius=1.5
  constraints (6):
    c: PointOnObject(g0,g-1)
    c: PointOnObject(g1,g-1)
    c: DistanceX(g0,g1) = 110
    c: Diameter(g1) = 3
    c: Equal(g1,g0)
    c: DistanceX(g-1,g0) = 15
FEATURE [PartDesign::Hole] Hole004
  BaseFeature = -> Hole003
  CustomThreadClearance = 0
  Depth = 14
  DepthType = 0
  Diameter = 2.5
  DrillForDepth = false
  DrillPoint = 0
  DrillPointAngle = 118
  HoleCutCountersinkAngle = 90
  HoleCutCustomValues = false
  HoleCutDepth = 0
  HoleCutDiameter = 6.1
  HoleCutType = 0
  ModelThread = false
  Profile = -> Sketch021
  Refine = true
  Suppressed = false
  Tapered = false
  TaperedAngle = 90
  ThreadClass = 0
  ThreadDepth = 14
  ThreadDepthType = 0
  ThreadDirection = 0
  ThreadFit = 0
  ThreadSize = 9
  ThreadType = 1
  Threaded = true
  UseCustomThreadClearance = false
FEATURE [PartDesign::Body] Body  label="FrameUpper"
  AllowCompound = false
  Group = -> [Sketch,Pad,DatumPlane,Sketch001,Pad001,DatumPlane001,Sketch002,Sketch003,Pad002,Pocket,Sketch004,Sketch005,Pocket002,Pocket003,Sketch006,Pocket004,Sketch007,Pocket005,Sketch008,Pocket006,Sketch009,Pocket007,Sketch010,Pocket008,Sketch011,Hole,Sketch012,Pocket009,Sketch013,Pocket010,Sketch014,Pocket011,Sketch015,Sketch020,Pocket013,Hole001,Sketch016,Hole002,Sketch018,Hole003,Sketch021,Hole004]
  Origin = -> Origin001
  Tip = -> Hole004
COMPONENT P1 — geometry summary ("FrameUpperAssembly"; no construction recipe available for this part):
  bounding box: 310.0 x 94.9 x 18.0 mm
  tessellated surface: 10,726 triangles
  volume: 131386 mm^3 (25% of its bounding box)
PROVENANCE & LICENSES
A FreeCAD (.FCStd) document from a public repository crawl; recipes are the document's own serialized feature recipes (and, for linked parts, companion documents' recipes).
License: as declared in the source repository (recorded in the dataset sidecar).
